# Revit family: WH1847B
name_source: partatom
category: Mechanical Equipment
revit_build: Autodesk Revit MEP 2016 (Build: 20150220_1215(x64)
units: mm (PartAtom-declared; Revit-internal decimal feet)

## family parameters
Cut with Voids When Loaded = No
Host = Face
OmniClass Number = 23.65.70.14.11
OmniClass Title = Drinking Fountains/Coolers
Part Type = Normal
Room Calculation Point = No
Round Connector Dimension = Use Diameter
Shared = Yes

## types (1)
- WH1847B
    Amperage = 0
    CW Connection = No
    Default Elevation = 36 "
    Description = Ligature -Resistant Spindle Button Surface Mount Toilet Paper Holder
    HW Connection = No
    Manufacturer = Whitehall Mfg
    Material = Stainless Steel
    Model = WH1847B
    OVERALL DEPTH = 10
    OVERALL SIZE HEIGHT = 4.5
    OVERALL SIZE WIDTH = 10.75
    Revised Date = 10/03/19
    Tempered Water Connection = No
    URL = https://www.whitehallmfg.com
    Vent Connection = No
    Voltage = 0
    Waste Connection = No

## geometry (parser evidence)
native form markers: Sweep x3
no freeform markers — native parametric forms only
